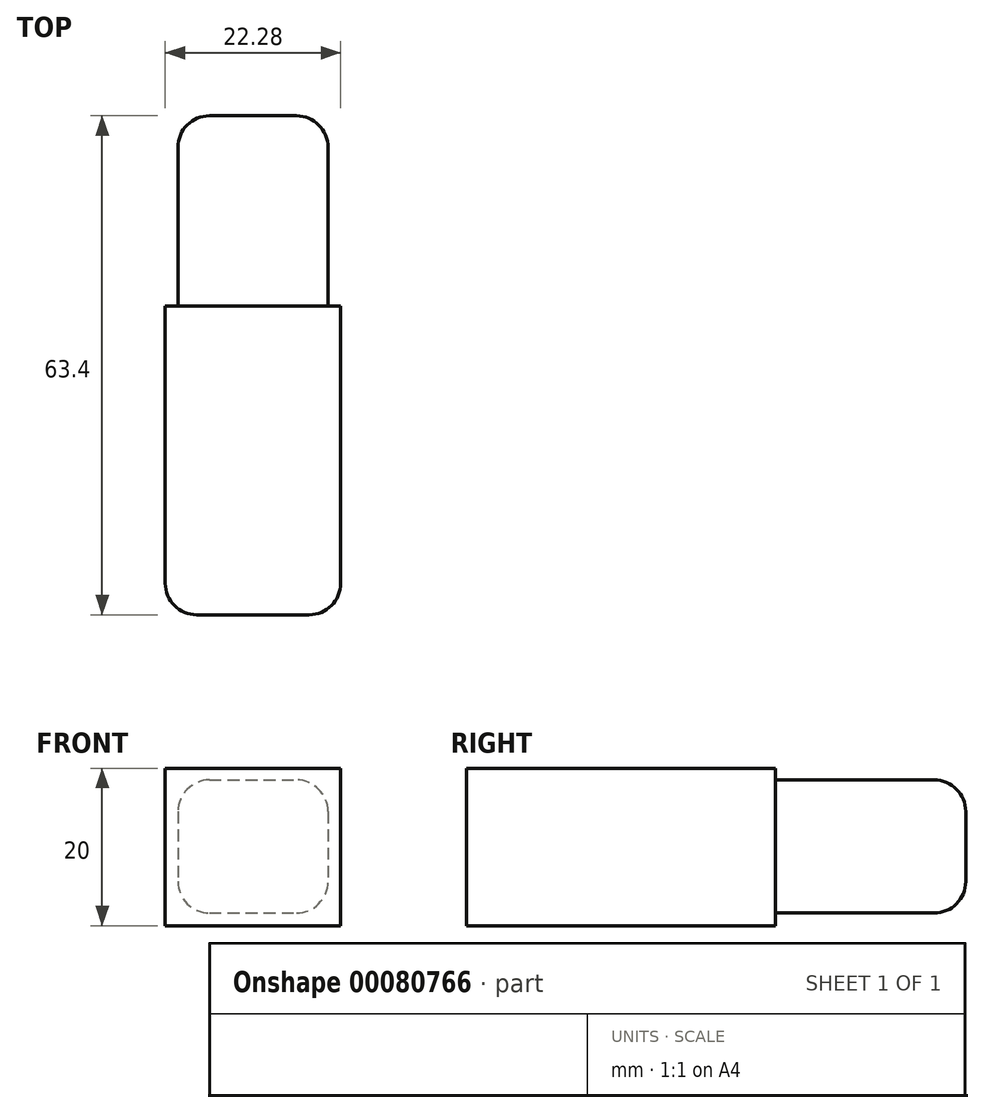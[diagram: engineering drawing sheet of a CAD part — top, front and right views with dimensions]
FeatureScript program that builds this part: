
annotation { "Feature Type Name" : "Feature", "Feature Type Description" : "" }
export const myFeature = defineFeature(function(context is Context, id is Id, definition is map)
    precondition{}
    {
        {
            var Q0;
            Q0=qCreatedBy(makeId("Top.planeOp"),FACE);
            var sketch = newSketch(context, id + "F0", { "sketchPlane" : qUnion([Q0])});
            skLineSegment(sketch, "E0.bottom", {"start": v(11.14, 19.6) * mm, "end": v(-11.14, 19.6) * mm});
            skLineSegment(sketch, "E0.top", {"start": v(11.14, -19.6) * mm, "end": v(-11.14, -19.6) * mm});
            skLineSegment(sketch, "E0.left", {"start": v(11.14, 19.6) * mm, "end": v(11.14, -19.6) * mm});
            skLineSegment(sketch, "E0.right", {"start": v(-11.14, 19.6) * mm, "end": v(-11.14, -19.6) * mm});
            skPoint(sketch, "E0.middle", {"position": v(0, 0) * mm});
            skSolve(sketch);
        }
        {
            var Q0;
            Q0 = qSketchRegion(id + "F0", true);
            extrude(context, id + "F1", {"entities" : qUnion([Q0]), "depth" : 20 * mm});
        }
        {
            var Q0;
            Q0=makeQuery(id+"F1.opExtrude","SWEPT_EDGE",EDGE,{"disambiguationData":[OSD([sQuery(id+"F0.wireOp",EDGE,"E0.top"),sQuery(id+"F0.wireOp",EDGE,"E0.right")])]});
            var Q1;
            Q1=makeQuery(id+"F1.opExtrude","SWEPT_EDGE",EDGE,{"disambiguationData":[OSD([sQuery(id+"F0.wireOp",EDGE,"E0.top"),sQuery(id+"F0.wireOp",EDGE,"E0.left")])]});
            fillet(context, id + "F2", {"entities" : qUnion([Q0, Q1]), "radius" : 4 * mm, "tangentPropagation" : true, "allowEdgeOverflow" : false});
        }
        {
            var Q0;
            Q0=makeQuery(id+"F1.opExtrude","SWEPT_FACE",FACE,{"disambiguationData":[OSD([sQuery(id+"F0.wireOp",EDGE,"E0.bottom")])]});
            var sketch = newSketch(context, id + "F3", { "sketchPlane" : qUnion([Q0])});
            skLineSegment(sketch, "E1.bottom", {"start": v(9.53, 18.52) * mm, "end": v(-9.53, 18.52) * mm});
            skLineSegment(sketch, "E1.top", {"start": v(9.53, 1.62) * mm, "end": v(-9.53, 1.62) * mm});
            skLineSegment(sketch, "E1.left", {"start": v(9.53, 18.52) * mm, "end": v(9.53, 1.62) * mm});
            skLineSegment(sketch, "E1.right", {"start": v(-9.53, 18.52) * mm, "end": v(-9.53, 1.62) * mm});
            skPoint(sketch, "E1.middle", {"position": v(0, 10.07) * mm});
            skSolve(sketch);
        }
        {
            var Q0;
            Q0=makeQuery(id+"F3.imprint","IMPRINT",FACE,{"disambiguationData":[TD([[makeQuery(id+"F3.imprint","IMPRINT",EDGE,{"derivedFrom":sQuery(id+"F3.wireOp",EDGE,"E1.bottom")}),1.0]])]});
            extrude(context, id + "F4", {"entities" : qUnion([Q0]), "operationType" : NewBodyOperationType.ADD, "depth" : 24.2 * mm});
        }
        {
            var Q0;
            Q0=makeQuery(id+"F4.opExtrude","SWEPT_EDGE",EDGE,{"disambiguationData":[OSD([sQuery(id+"F3.wireOp",EDGE,"E1.top"),sQuery(id+"F3.wireOp",EDGE,"E1.left")])]});
            var Q1;
            Q1=makeQuery(id+"F4.opExtrude","SWEPT_EDGE",EDGE,{"disambiguationData":[OSD([sQuery(id+"F3.wireOp",EDGE,"E1.top"),sQuery(id+"F3.wireOp",EDGE,"E1.right")])]});
            var Q2;
            Q2=makeQuery(id+"F4.opExtrude","SWEPT_EDGE",EDGE,{"disambiguationData":[OSD([sQuery(id+"F3.wireOp",EDGE,"E1.bottom"),sQuery(id+"F3.wireOp",EDGE,"E1.left")])]});
            var Q3;
            Q3=makeQuery(id+"F4.opExtrude","SWEPT_EDGE",EDGE,{"disambiguationData":[OSD([sQuery(id+"F3.wireOp",EDGE,"E1.bottom"),sQuery(id+"F3.wireOp",EDGE,"E1.right")])]});
            fillet(context, id + "F5", {"entities" : qUnion([Q0, Q1, Q2, Q3]), "radius" : 4 * mm, "tangentPropagation" : true, "allowEdgeOverflow" : false});
        }
        {
            var Q0;
            Q0=makeQuery(id+"F4.opExtrude","CAP_EDGE",EDGE,{"disambiguationData":[OSD([sQuery(id+"F3.wireOp",EDGE,"E1.right")])],"isStart":false});
            var Q1;
            Q1=makeQuery(id+"F4.opExtrude","CAP_EDGE",EDGE,{"disambiguationData":[OSD([sQuery(id+"F3.wireOp",EDGE,"E1.bottom")])],"isStart":false});
            var Q2;
            Q2=makeQuery(id+"F4.opExtrude","CAP_EDGE",EDGE,{"disambiguationData":[OSD([sQuery(id+"F3.wireOp",EDGE,"E1.left")])],"isStart":false});
            var Q3;
            Q3=makeQuery(id+"F4.opExtrude","CAP_EDGE",EDGE,{"disambiguationData":[OSD([sQuery(id+"F3.wireOp",EDGE,"E1.top")])],"isStart":false});
            fillet(context, id + "F6", {"entities" : qUnion([Q0, Q1, Q2, Q3]), "radius" : 4 * mm, "tangentPropagation" : true, "allowEdgeOverflow" : false});
        }
    });
